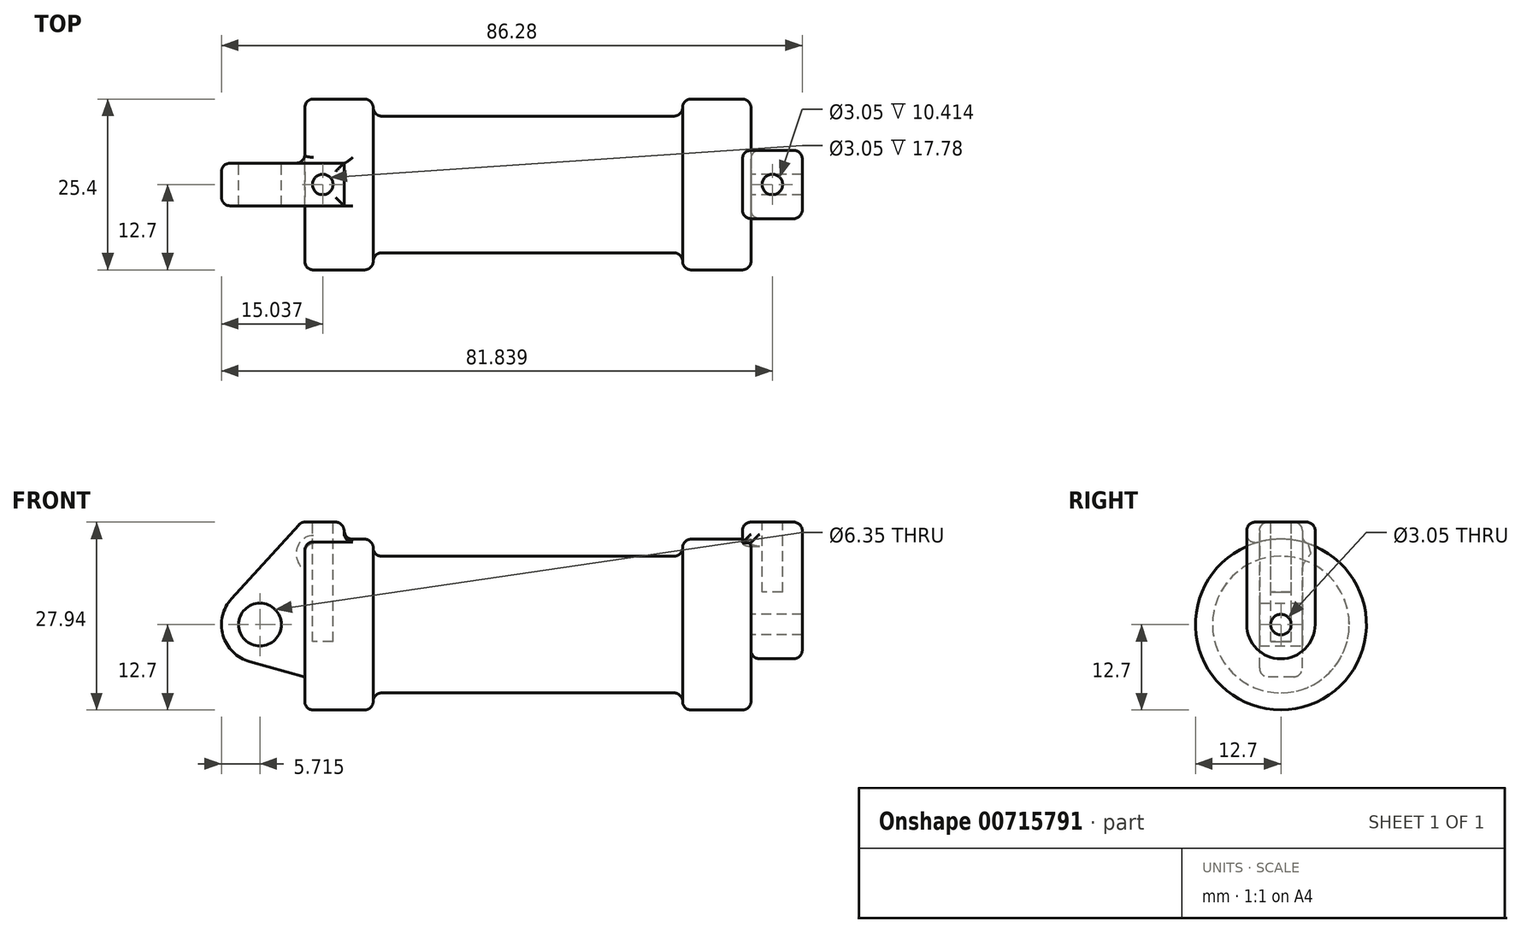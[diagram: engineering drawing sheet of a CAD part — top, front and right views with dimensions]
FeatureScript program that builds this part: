
annotation { "Feature Type Name" : "Feature", "Feature Type Description" : "" }
export const myFeature = defineFeature(function(context is Context, id is Id, definition is map)
    precondition{}
    {
        {
            var Q0;
            Q0=qCreatedBy(makeId("Front.planeOp"),FACE);
            var sketch = newSketch(context, id + "F0", { "sketchPlane" : qUnion([Q0])});
            skLineSegment(sketch, "E0", {"start": v(0, 0) * mm, "end": v(0, 12.7) * mm});
            skLineSegment(sketch, "E1", {"start": v(0, 12.7) * mm, "end": v(10.16, 12.7) * mm});
            skLineSegment(sketch, "E2", {"start": v(10.16, 12.7) * mm, "end": v(10.16, 10.16) * mm});
            skLineSegment(sketch, "E3", {"start": v(10.16, 10.16) * mm, "end": v(56.13, 10.16) * mm});
            skLineSegment(sketch, "E4", {"start": v(56.13, 10.16) * mm, "end": v(56.13, 12.7) * mm});
            skLineSegment(sketch, "E5", {"start": v(56.13, 12.7) * mm, "end": v(66.3, 12.7) * mm});
            skLineSegment(sketch, "E6", {"start": v(66.3, 12.7) * mm, "end": v(66.3, 0) * mm});
            skLineSegment(sketch, "E7", {"start": v(66.3, 0) * mm, "end": v(0, 0) * mm});
            skLineSegment(sketch, "E8", {"start": v(5.84, 15.24) * mm, "end": v(-0.5, 15.24) * mm});
            skLineSegment(sketch, "E9", {"start": v(-0.5, 15.24) * mm, "end": v(-10.88, 3.85) * mm});
            skLineSegment(sketch, "E10", {"start": v(0, 0) * mm, "end": v(-6.65, 0) * mm});
            skCircle(sketch, "E11", {"center": v(-6.65, 0) * mm, "radius": 5.72 * mm});
            skCircle(sketch, "E12", {"center": v(-6.65, 0) * mm, "radius": 3.18 * mm});
            skLineSegment(sketch, "E13", {"start": v(5.84, 15.24) * mm, "end": v(5.84, -9.4) * mm});
            skLineSegment(sketch, "E14", {"start": v(5.84, -9.4) * mm, "end": v(-8.18, -5.5) * mm});
            skSolve(sketch);
        }
        {
            var Q0;
            {var subQ0=sQuery(id+"F0.wireOp",EDGE,"E2");Q0=makeQuery(id+"F0.imprint","IMPRINT",FACE,{"disambiguationData":[TD([[makeQuery(id+"F0.imprint","IMPRINT",EDGE,{"derivedFrom":subQ0}),-1.0]])]});}
            var Q1;
            {var subQ0=sQuery(id+"F0.wireOp",EDGE,"E0");Q1=makeQuery(id+"F0.imprint","IMPRINT",FACE,{"disambiguationData":[TD([[makeQuery(id+"F0.imprint","IMPRINT",EDGE,{"derivedFrom":subQ0}),-1.0]])]});}
            var Q2;
            Q2=sQuery(id+"F0.wireOp",EDGE,"E7");
            revolve(context, id + "F1", {"entities" : qUnion([Q0, Q1]), "axis" : qUnion([Q2]), "revolveType" : RevolveType.FULL});
        }
        {
            var Q0;
            {var subQ0=sQuery(id+"F0.wireOp",EDGE,"E14");Q0=makeQuery(id+"F0.imprint","IMPRINT",FACE,{"disambiguationData":[TD([[makeQuery(id+"F0.imprint","IMPRINT",EDGE,{"derivedFrom":subQ0}),-1.0]])]});}
            var Q1;
            {var subQ1=sQuery(id+"F0.wireOp",EDGE,"E0");Q1=makeQuery(id+"F0.imprint","IMPRINT",FACE,{"disambiguationData":[TD([[makeQuery(id+"F0.imprint","IMPRINT",EDGE,{"derivedFrom":subQ1}),1.0]])]});}
            var Q2;
            {var subQ5=sQuery(id+"F0.wireOp",EDGE,"E12");Q2=makeQuery(id+"F0.imprint","IMPRINT",FACE,{"disambiguationData":[TD([[makeQuery(id+"F0.imprint","IMPRINT",EDGE,{"derivedFrom":subQ5}),-1.0]])]});}
            var Q3;
            {var subQ0=sQuery(id+"F0.wireOp",EDGE,"E0");Q3=makeQuery(id+"F0.imprint","IMPRINT",FACE,{"disambiguationData":[TD([[makeQuery(id+"F0.imprint","IMPRINT",EDGE,{"derivedFrom":subQ0}),-1.0]])]});}
            extrude(context, id + "F2", {"entities" : qUnion([Q0, Q1, Q2, Q3]), "endBound" : BoundingType.SYMMETRIC, "depth" : 6.35 * mm, "offsetDistance" : 25.4 * mm});
        }
        {
            var Q0;
            Q0=makeQuery(id+"F2.opExtrude","SWEPT_BODY",BODY,{"disambiguationData":[OSD([sQuery(id+"F0.wireOp",EDGE,"E8"),sQuery(id+"F0.wireOp",EDGE,"E9"),sQuery(id+"F0.wireOp",EDGE,"E11"),sQuery(id+"F0.wireOp",EDGE,"E12"),sQuery(id+"F0.wireOp",EDGE,"E13"),sQuery(id+"F0.wireOp",EDGE,"E14")])]});
            var Q1;
            Q1=makeQuery(id+"F1.opRevolve","SWEPT_BODY",BODY,{"disambiguationData":[OSD([sQuery(id+"F0.wireOp",EDGE,"E0"),sQuery(id+"F0.wireOp",EDGE,"E1"),sQuery(id+"F0.wireOp",EDGE,"E2"),sQuery(id+"F0.wireOp",EDGE,"E3"),sQuery(id+"F0.wireOp",EDGE,"E4"),sQuery(id+"F0.wireOp",EDGE,"E5"),sQuery(id+"F0.wireOp",EDGE,"E6"),sQuery(id+"F0.wireOp",EDGE,"E7")])]});
            booleanBodies(context, id + "F3", {"operationType" : BooleanOperationType.UNION, "tools" : qUnion([Q0, Q1])});
        }
        {
            var Q0;
            Q0=makeQuery(id+"F1.opRevolve","SWEPT_FACE",FACE,{"disambiguationData":[OSD([sQuery(id+"F0.wireOp",EDGE,"E6")])]});
            var sketch = newSketch(context, id + "F4", { "sketchPlane" : qUnion([Q0])});
            skCircle(sketch, "E15.0.0", {"center": v(0, 0) * mm, "radius": 12.7 * mm});
            skCircle(sketch, "E16", {"center": v(0, 0) * mm, "radius": 1.52 * mm});
            skCircle(sketch, "E17", {"center": v(0, 0) * mm, "radius": 5.08 * mm});
            skLineSegment(sketch, "E18", {"start": v(-5.08, 0) * mm, "end": v(-5.08, 15.24) * mm});
            skLineSegment(sketch, "E19", {"start": v(-5.08, 15.24) * mm, "end": v(5.08, 15.24) * mm});
            skLineSegment(sketch, "E20", {"start": v(5.08, 15.24) * mm, "end": v(5.08, 0) * mm});
            skSolve(sketch);
        }
        {
            var Q0;
            {var subQ5=sQuery(id+"F4.wireOp",EDGE,"E19");Q0=makeQuery(id+"F4.imprint","IMPRINT",FACE,{"disambiguationData":[TD([[makeQuery(id+"F4.imprint","IMPRINT",EDGE,{"derivedFrom":subQ5}),-1.0]])]});}
            extrude(context, id + "F5", {"entities" : qUnion([Q0]), "oppositeDirection" : true, "depth" : 1.27 * mm, "offsetDistance" : 25.4 * mm});
        }
        {
            var Q0;
            {var subQ0=sQuery(id+"F4.wireOp",EDGE,"E18");var subQ1=sQuery(id+"F4.wireOp",EDGE,"E15.0.0");var subQ2=makeQuery(id+"F4.imprint","INTERSECT",VERTEX,{"derivedFrom":[subQ1,subQ0]});Q0=makeQuery(id+"F4.imprint","IMPRINT",FACE,{"disambiguationData":[TD([[makeQuery(id+"F4.imprint","IMPRINT",EDGE,{"disambiguationData":[TD([[subQ2,1.0]])],"derivedFrom":subQ1}),1.0]])]});}
            var Q1;
            {var subQ5=sQuery(id+"F4.wireOp",EDGE,"E19");Q1=makeQuery(id+"F4.imprint","IMPRINT",FACE,{"disambiguationData":[TD([[makeQuery(id+"F4.imprint","IMPRINT",EDGE,{"derivedFrom":subQ5}),-1.0]])]});}
            var Q2;
            Q2=makeQuery(id+"F4.imprint","IMPRINT",FACE,{"disambiguationData":[TD([[makeQuery(id+"F4.imprint","IMPRINT",EDGE,{"derivedFrom":sQuery(id+"F4.wireOp",EDGE,"E16")}),-1.0]])]});
            extrude(context, id + "F6", {"entities" : qUnion([Q0, Q1, Q2]), "depth" : 7.62 * mm, "offsetDistance" : 25.4 * mm});
        }
        {
            var Q0;
            Q0=makeQuery(id+"F5.opExtrude","SWEPT_BODY",BODY,{"disambiguationData":[OSD([sQuery(id+"F4.wireOp",EDGE,"E15.0.0"),sQuery(id+"F4.wireOp",EDGE,"E18"),sQuery(id+"F4.wireOp",EDGE,"E19"),sQuery(id+"F4.wireOp",EDGE,"E20")])]});
            var Q1;
            Q1=makeQuery(id+"F6.opExtrude","SWEPT_BODY",BODY,{"disambiguationData":[OSD([sQuery(id+"F4.wireOp",EDGE,"E16"),sQuery(id+"F4.wireOp",EDGE,"E17"),sQuery(id+"F4.wireOp",EDGE,"E18"),sQuery(id+"F4.wireOp",EDGE,"E19"),sQuery(id+"F4.wireOp",EDGE,"E20")])]});
            booleanBodies(context, id + "F7", {"operationType" : BooleanOperationType.UNION, "tools" : qUnion([Q0, Q1])});
        }
        {
            var Q0;
            {var subQ0=sQuery(id+"F4.wireOp",EDGE,"E19");Q0=makeQuery(id+"F7.opBoolean","MERGE",FACE,{"derivedFrom":[makeQuery(id+"F5.opExtrude","SWEPT_FACE",FACE,{"disambiguationData":[OSD([subQ0])]}),makeQuery(id+"F6.opExtrude","SWEPT_FACE",FACE,{"disambiguationData":[OSD([subQ0])]})]});}
            var sketch = newSketch(context, id + "F8", { "sketchPlane" : qUnion([Q0])});
            skCircle(sketch, "E21", {"center": v(69.47, 0) * mm, "radius": 1.52 * mm});
            skPoint(sketch, "E21.centerSnap0", {"position": v(73.91, 0) * mm});
            skPoint(sketch, "E21.centerSnap1", {"position": v(69.47, -5.08) * mm});
            skSolve(sketch);
        }
        {
            var Q0;
            Q0 = qSketchRegion(id + "F8", true);
            extrude(context, id + "F9", {"entities" : qUnion([Q0]), "operationType" : NewBodyOperationType.REMOVE, "oppositeDirection" : true, "depth" : 10.4 * mm, "offsetDistance" : 25.4 * mm});
        }
        {
            var Q0;
            Q0=makeQuery(id+"F2.opExtrude","SWEPT_FACE",FACE,{"disambiguationData":[OSD([sQuery(id+"F0.wireOp",EDGE,"E8")])]});
            var sketch = newSketch(context, id + "F10", { "sketchPlane" : qUnion([Q0])});
            skCircle(sketch, "E22", {"center": v(2.67, 0) * mm, "radius": 1.52 * mm});
            skPoint(sketch, "E22.centerSnap1", {"position": v(5.84, 0) * mm});
            skSolve(sketch);
        }
        {
            var Q0;
            Q0=makeQuery(id+"F10.imprint","IMPRINT",FACE,{"disambiguationData":[TD([[makeQuery(id+"F10.imprint","IMPRINT",EDGE,{"derivedFrom":sQuery(id+"F10.wireOp",EDGE,"E22")}),1.0]])]});
            var Q1;
            Q1=sQuery(id+"F10.wireOp",EDGE,"E22");
            extrude(context, id + "F11", {"entities" : qUnion([Q0]), "operationType" : NewBodyOperationType.REMOVE, "surfaceEntities" : qUnion([Q1]), "oppositeDirection" : true, "depth" : 17.78 * mm, "offsetDistance" : 25.4 * mm});
        }
        {
            var Q0;
            Q0=makeQuery(id+"F1.opRevolve","SWEPT_FACE",FACE,{"disambiguationData":[OSD([sQuery(id+"F0.wireOp",EDGE,"E3")])]});
            fillet(context, id + "F12", {"entities" : qUnion([Q0]), "radius" : 1.27 * mm, "tangentPropagation" : true, "allowEdgeOverflow" : false});
        }
        {
            var Q0;
            Q0=makeQuery(id+"F1.opRevolve","SWEPT_EDGE",EDGE,{"disambiguationData":[OSD([sQuery(id+"F0.wireOp",EDGE,"E5"),sQuery(id+"F0.wireOp",EDGE,"E6")])]});
            var Q1;
            Q1=makeQuery(id+"F1.opRevolve","SWEPT_EDGE",EDGE,{"disambiguationData":[OSD([sQuery(id+"F0.wireOp",EDGE,"E4"),sQuery(id+"F0.wireOp",EDGE,"E5")])]});
            var Q2;
            Q2=makeQuery(id+"F6.opExtrude","CAP_EDGE",EDGE,{"disambiguationData":[OSD([sQuery(id+"F4.wireOp",EDGE,"E20")])],"isStart":true});
            var Q3;
            Q3=makeQuery(id+"F6.opExtrude","CAP_EDGE",EDGE,{"disambiguationData":[OSD([sQuery(id+"F4.wireOp",EDGE,"E17")])],"isStart":true});
            var Q4;
            Q4=makeQuery(id+"F6.opExtrude","CAP_EDGE",EDGE,{"disambiguationData":[OSD([sQuery(id+"F4.wireOp",EDGE,"E18")])],"isStart":false});
            var Q5;
            Q5=makeQuery(id+"F6.opExtrude","CAP_EDGE",EDGE,{"disambiguationData":[OSD([sQuery(id+"F4.wireOp",EDGE,"E20")])],"isStart":false});
            var Q6;
            {var subQ0=sQuery(id+"F4.wireOp",EDGE,"E19");var subQ1=sQuery(id+"F4.wireOp",EDGE,"E18");Q6=makeQuery(id+"F7.opBoolean","MERGE",EDGE,{"derivedFrom":[makeQuery(id+"F5.opExtrude","SWEPT_EDGE",EDGE,{"disambiguationData":[OSD([subQ1,subQ0])]}),makeQuery(id+"F6.opExtrude","SWEPT_EDGE",EDGE,{"disambiguationData":[OSD([subQ1,subQ0])]})]});}
            var Q7;
            {var subQ0=sQuery(id+"F4.wireOp",EDGE,"E20");var subQ1=sQuery(id+"F4.wireOp",EDGE,"E19");Q7=makeQuery(id+"F7.opBoolean","MERGE",EDGE,{"derivedFrom":[makeQuery(id+"F5.opExtrude","SWEPT_EDGE",EDGE,{"disambiguationData":[OSD([subQ1,subQ0])]}),makeQuery(id+"F6.opExtrude","SWEPT_EDGE",EDGE,{"disambiguationData":[OSD([subQ1,subQ0])]})]});}
            var Q8;
            Q8=makeQuery(id+"F5.opExtrude","CAP_EDGE",EDGE,{"disambiguationData":[OSD([sQuery(id+"F4.wireOp",EDGE,"E19")])],"isStart":false});
            var Q9;
            Q9=makeQuery(id+"F6.opExtrude","CAP_EDGE",EDGE,{"disambiguationData":[OSD([sQuery(id+"F4.wireOp",EDGE,"E19")])],"isStart":false});
            var Q10;
            Q10=makeQuery(id+"F5.opExtrude","CAP_EDGE",EDGE,{"disambiguationData":[OSD([sQuery(id+"F4.wireOp",EDGE,"E20")])],"isStart":false});
            var Q11;
            Q11=makeQuery(id+"F5.opExtrude","CAP_EDGE",EDGE,{"disambiguationData":[OSD([sQuery(id+"F4.wireOp",EDGE,"E18")])],"isStart":false});
            var Q12;
            Q12=makeQuery(id+"F5.opExtrude","SWEPT_EDGE",EDGE,{"disambiguationData":[OSD([sQuery(id+"F4.wireOp",EDGE,"E15.0.0"),sQuery(id+"F4.wireOp",EDGE,"E18")])]});
            fillet(context, id + "F13", {"entities" : qUnion([Q0, Q1, Q2, Q3, Q4, Q5, Q6, Q7, Q8, Q9, Q10, Q11, Q12]), "radius" : 1.27 * mm, "tangentPropagation" : true, "allowEdgeOverflow" : false});
        }
        {
            var Q0;
            Q0=makeQuery(id+"F1.opRevolve","SWEPT_EDGE",EDGE,{"disambiguationData":[OSD([sQuery(id+"F0.wireOp",EDGE,"E1"),sQuery(id+"F0.wireOp",EDGE,"E2")])]});
            var Q1;
            Q1=makeQuery(id+"F1.opRevolve","SWEPT_EDGE",EDGE,{"disambiguationData":[OSD([sQuery(id+"F0.wireOp",EDGE,"E0"),sQuery(id+"F0.wireOp",EDGE,"E1")])]});
            var Q2;
            Q2=makeQuery(id+"F3.opBoolean","INTERSECT",EDGE,{"derivedFrom":[makeQuery(id+"F1.opRevolve","SWEPT_FACE",FACE,{"disambiguationData":[OSD([sQuery(id+"F0.wireOp",EDGE,"E1")])]}),makeQuery(id+"F2.opExtrude","CAP_FACE",FACE,{"disambiguationData":[OSD([sQuery(id+"F0.wireOp",EDGE,"E8"),sQuery(id+"F0.wireOp",EDGE,"E9"),sQuery(id+"F0.wireOp",EDGE,"E11"),sQuery(id+"F0.wireOp",EDGE,"E12"),sQuery(id+"F0.wireOp",EDGE,"E13"),sQuery(id+"F0.wireOp",EDGE,"E14")])],"isStart":true})]});
            var Q3;
            Q3=makeQuery(id+"F2.opExtrude","CAP_EDGE",EDGE,{"disambiguationData":[OSD([sQuery(id+"F0.wireOp",EDGE,"E14")])],"isStart":true});
            var Q4;
            Q4=makeQuery(id+"F2.opExtrude","CAP_EDGE",EDGE,{"disambiguationData":[OSD([sQuery(id+"F0.wireOp",EDGE,"E8")])],"isStart":true});
            var Q5;
            Q5=makeQuery(id+"F2.opExtrude","SWEPT_EDGE",EDGE,{"disambiguationData":[OSD([sQuery(id+"F0.wireOp",EDGE,"E8"),sQuery(id+"F0.wireOp",EDGE,"E9")])]});
            var Q6;
            Q6=makeQuery(id+"F2.opExtrude","SWEPT_EDGE",EDGE,{"disambiguationData":[OSD([sQuery(id+"F0.wireOp",EDGE,"E8"),sQuery(id+"F0.wireOp",EDGE,"E13")])]});
            var Q7;
            Q7=makeQuery(id+"F2.opExtrude","CAP_EDGE",EDGE,{"disambiguationData":[OSD([sQuery(id+"F0.wireOp",EDGE,"E8")])],"isStart":false});
            var Q8;
            Q8=makeQuery(id+"F2.opExtrude","CAP_EDGE",EDGE,{"disambiguationData":[OSD([sQuery(id+"F0.wireOp",EDGE,"E9")])],"isStart":false});
            var Q9;
            Q9=makeQuery(id+"F2.opExtrude","CAP_EDGE",EDGE,{"disambiguationData":[OSD([sQuery(id+"F0.wireOp",EDGE,"E11")])],"isStart":false});
            var Q10;
            Q10=makeQuery(id+"F2.opExtrude","CAP_EDGE",EDGE,{"disambiguationData":[OSD([sQuery(id+"F0.wireOp",EDGE,"E11")])],"isStart":true});
            var Q11;
            Q11=makeQuery(id+"F3.opBoolean","INTERSECT",EDGE,{"derivedFrom":[makeQuery(id+"F1.opRevolve","SWEPT_FACE",FACE,{"disambiguationData":[OSD([sQuery(id+"F0.wireOp",EDGE,"E1")])]}),makeQuery(id+"F2.opExtrude","SWEPT_FACE",FACE,{"disambiguationData":[OSD([sQuery(id+"F0.wireOp",EDGE,"E13")])]})]});
            fillet(context, id + "F14", {"entities" : qUnion([Q0, Q1, Q2, Q3, Q4, Q5, Q6, Q7, Q8, Q9, Q10, Q11]), "radius" : 1.27 * mm, "tangentPropagation" : true, "allowEdgeOverflow" : false});
        }
    });
